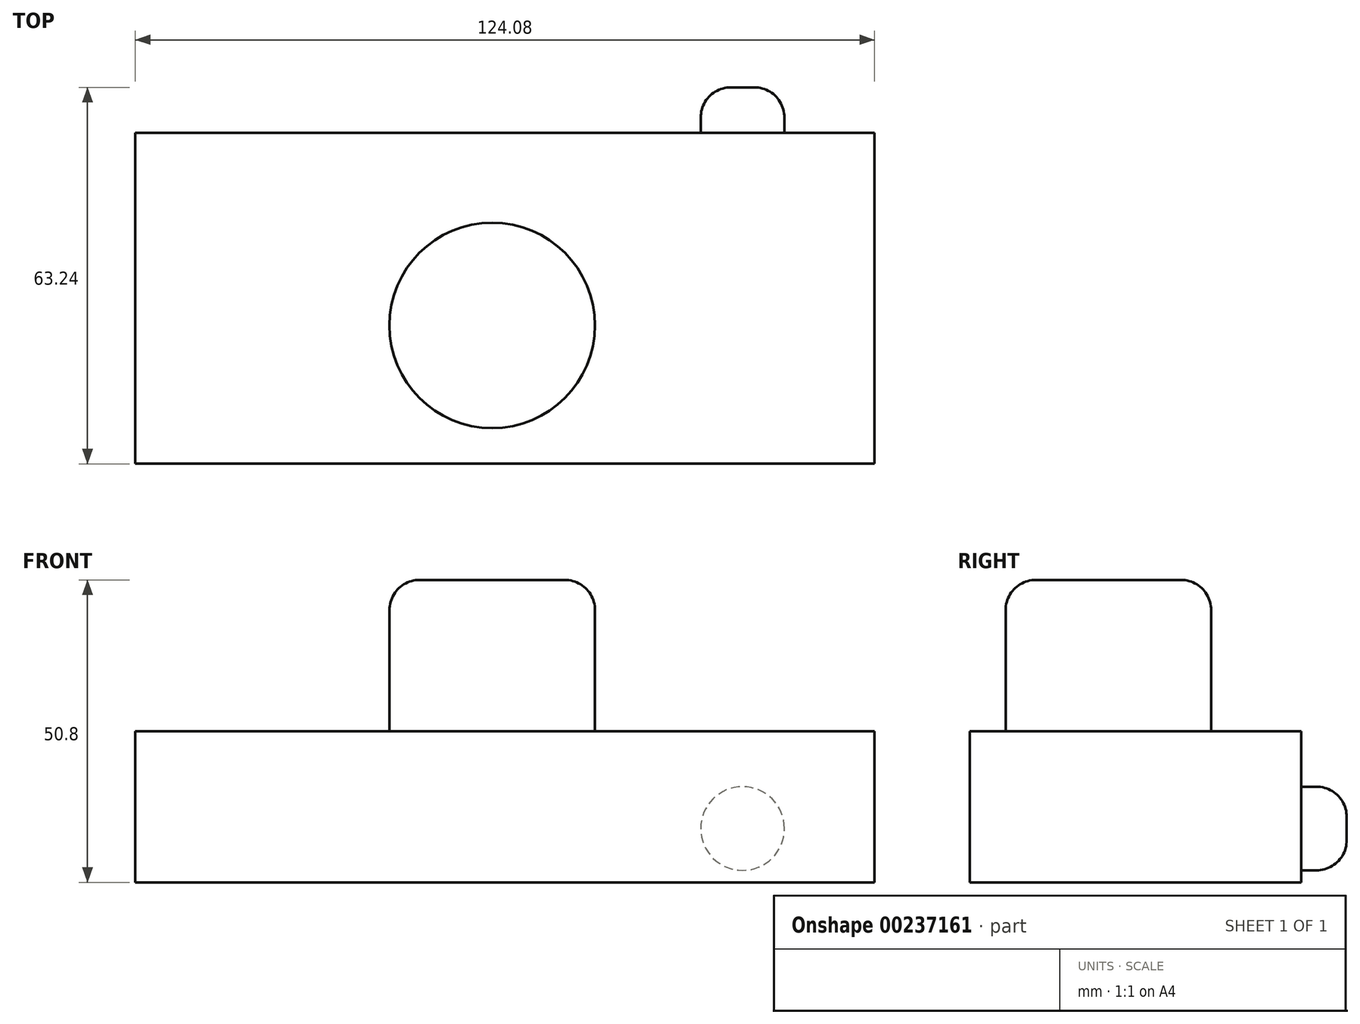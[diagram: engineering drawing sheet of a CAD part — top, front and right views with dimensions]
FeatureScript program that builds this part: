
annotation { "Feature Type Name" : "Feature", "Feature Type Description" : "" }
export const myFeature = defineFeature(function(context is Context, id is Id, definition is map)
    precondition{}
    {
        {
            var Q0;
            Q0=qCreatedBy(makeId("Top.planeOp"),FACE);
            var sketch = newSketch(context, id + "F0", { "sketchPlane" : qUnion([Q0])});
            skLineSegment(sketch, "E0.bottom", {"start": v(-59.9, -23.25) * mm, "end": v(64.18, -23.25) * mm});
            skLineSegment(sketch, "E0.top", {"start": v(-59.9, 32.37) * mm, "end": v(64.18, 32.37) * mm});
            skLineSegment(sketch, "E0.left", {"start": v(-59.9, -23.25) * mm, "end": v(-59.9, 32.37) * mm});
            skLineSegment(sketch, "E0.right", {"start": v(64.18, -23.25) * mm, "end": v(64.18, 32.37) * mm});
            skSolve(sketch);
        }
        {
            var Q0;
            Q0=makeQuery(id+"F0.imprint","IMPRINT",FACE,{"disambiguationData":[TD([[makeQuery(id+"F0.imprint","IMPRINT",EDGE,{"derivedFrom":sQuery(id+"F0.wireOp",EDGE,"E0.bottom")}),1.0]])]});
            extrude(context, id + "F1", {"entities" : qUnion([Q0]), "depth" : 25.4 * mm});
        }
        {
            var Q0;
            Q0=makeQuery(id+"F1.opExtrude","CAP_FACE",FACE,{"disambiguationData":[OSD([sQuery(id+"F0.wireOp",EDGE,"E0.bottom"),sQuery(id+"F0.wireOp",EDGE,"E0.top"),sQuery(id+"F0.wireOp",EDGE,"E0.left"),sQuery(id+"F0.wireOp",EDGE,"E0.right")])],"isStart":false});
            var sketch = newSketch(context, id + "F2", { "sketchPlane" : qUnion([Q0])});
            skCircle(sketch, "E1", {"center": v(0, 0) * mm, "radius": 17.25 * mm});
            skSolve(sketch);
        }
        {
            var Q0;
            Q0=makeQuery(id+"F2.imprint","IMPRINT",FACE,{"disambiguationData":[TD([[makeQuery(id+"F2.imprint","IMPRINT",EDGE,{"derivedFrom":sQuery(id+"F2.wireOp",EDGE,"E1")}),1.0]])]});
            extrude(context, id + "F3", {"entities" : qUnion([Q0]), "operationType" : NewBodyOperationType.ADD, "depth" : 25.4 * mm});
        }
        {
            var Q0;
            Q0=makeQuery(id+"F3.opExtrude","CAP_EDGE",EDGE,{"disambiguationData":[OSD([sQuery(id+"F2.wireOp",EDGE,"E1")])],"isStart":false});
            fillet(context, id + "F4", {"entities" : qUnion([Q0]), "radius" : 5.08 * mm, "tangentPropagation" : true, "allowEdgeOverflow" : false});
        }
        {
            var Q0;
            Q0=makeQuery(id+"F1.opExtrude","SWEPT_FACE",FACE,{"disambiguationData":[OSD([sQuery(id+"F0.wireOp",EDGE,"E0.top")])]});
            var sketch = newSketch(context, id + "F5", { "sketchPlane" : qUnion([Q0])});
            skCircle(sketch, "E2", {"center": v(-42.03, 9.04) * mm, "radius": 7.02 * mm});
            skSolve(sketch);
        }
        {
            var Q0;
            Q0=makeQuery(id+"F5.imprint","IMPRINT",FACE,{"disambiguationData":[TD([[makeQuery(id+"F5.imprint","IMPRINT",EDGE,{"derivedFrom":sQuery(id+"F5.wireOp",EDGE,"E2")}),1.0]])]});
            extrude(context, id + "F6", {"entities" : qUnion([Q0]), "operationType" : NewBodyOperationType.ADD, "depth" : 7.62 * mm});
        }
        {
            var Q0;
            Q0=makeQuery(id+"F6.opExtrude","CAP_EDGE",EDGE,{"disambiguationData":[OSD([sQuery(id+"F5.wireOp",EDGE,"E2")])],"isStart":false});
            fillet(context, id + "F7", {"entities" : qUnion([Q0]), "radius" : 5.08 * mm, "tangentPropagation" : true, "allowEdgeOverflow" : false});
        }
    });
